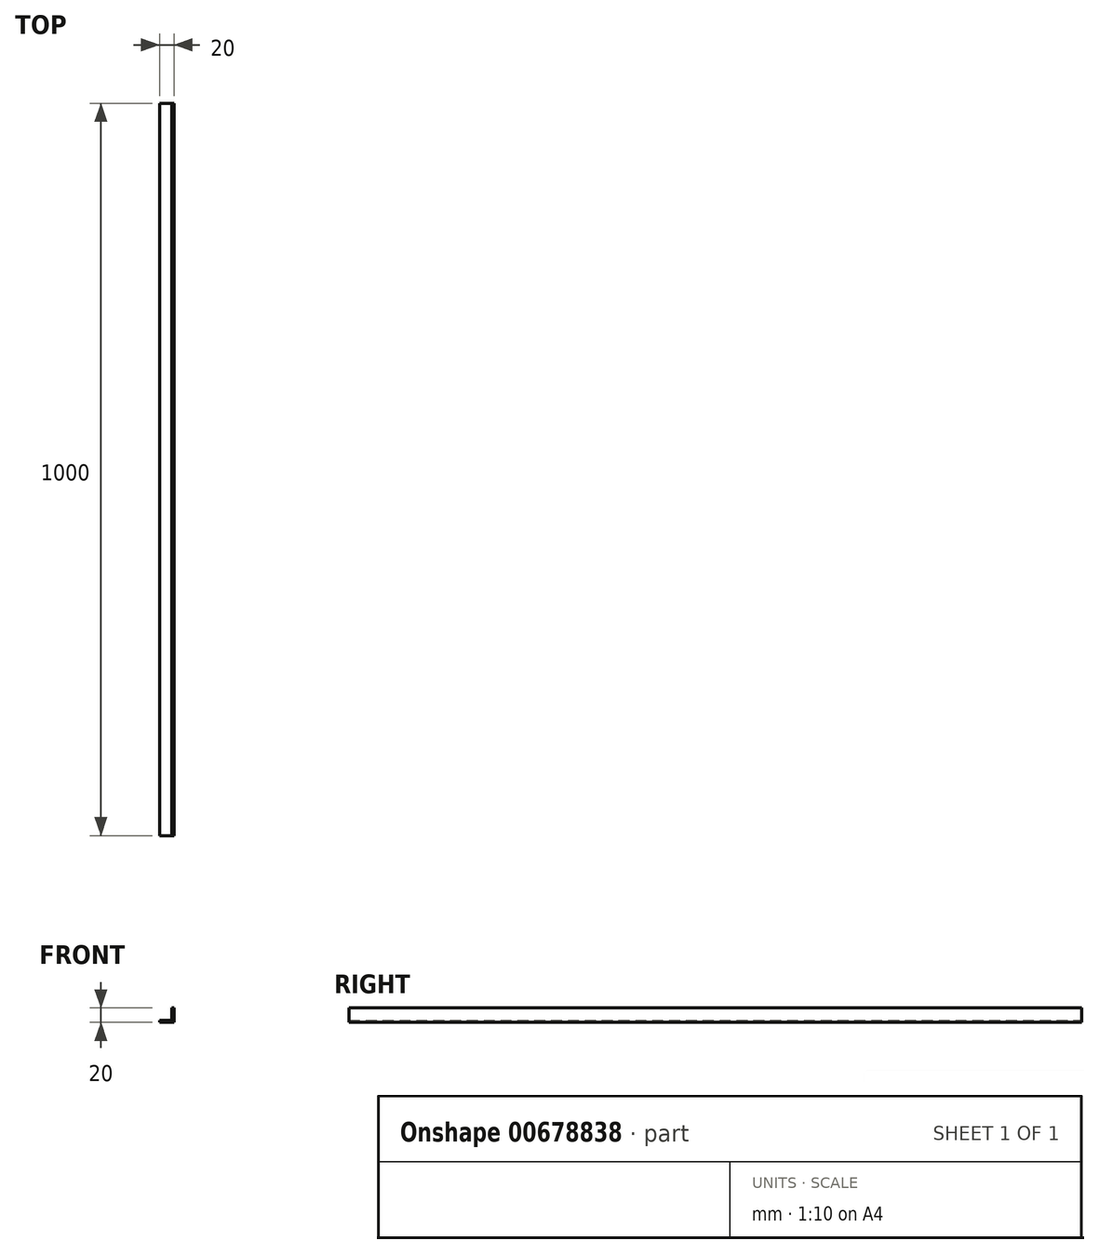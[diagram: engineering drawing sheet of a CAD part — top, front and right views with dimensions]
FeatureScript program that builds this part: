
annotation { "Feature Type Name" : "Feature", "Feature Type Description" : "" }
export const myFeature = defineFeature(function(context is Context, id is Id, definition is map)
    precondition{}
    {
        {
            var Q0;
            Q0=qCreatedBy(makeId("Front.planeOp"),FACE);
            var sketch = newSketch(context, id + "F0", { "sketchPlane" : qUnion([Q0])});
            skLineSegment(sketch, "E0", {"start": v(0, 0) * mm, "end": v(20, 0) * mm});
            skLineSegment(sketch, "E1", {"start": v(20, 0) * mm, "end": v(20, 20) * mm});
            skLineSegment(sketch, "E2", {"start": v(20, 20) * mm, "end": v(17, 20) * mm});
            skLineSegment(sketch, "E3", {"start": v(17, 20) * mm, "end": v(17, 3) * mm});
            skLineSegment(sketch, "E4", {"start": v(17, 3) * mm, "end": v(0, 3) * mm});
            skLineSegment(sketch, "E5", {"start": v(0, 3) * mm, "end": v(0, 0) * mm});
            skSolve(sketch);
        }
        {
            var Q0;
            Q0 = qSketchRegion(id + "F0", true);
            extrude(context, id + "F1", {"entities" : qUnion([Q0]), "depth" : 1000 * mm, "offsetDistance" : 25 * mm});
        }
    });
